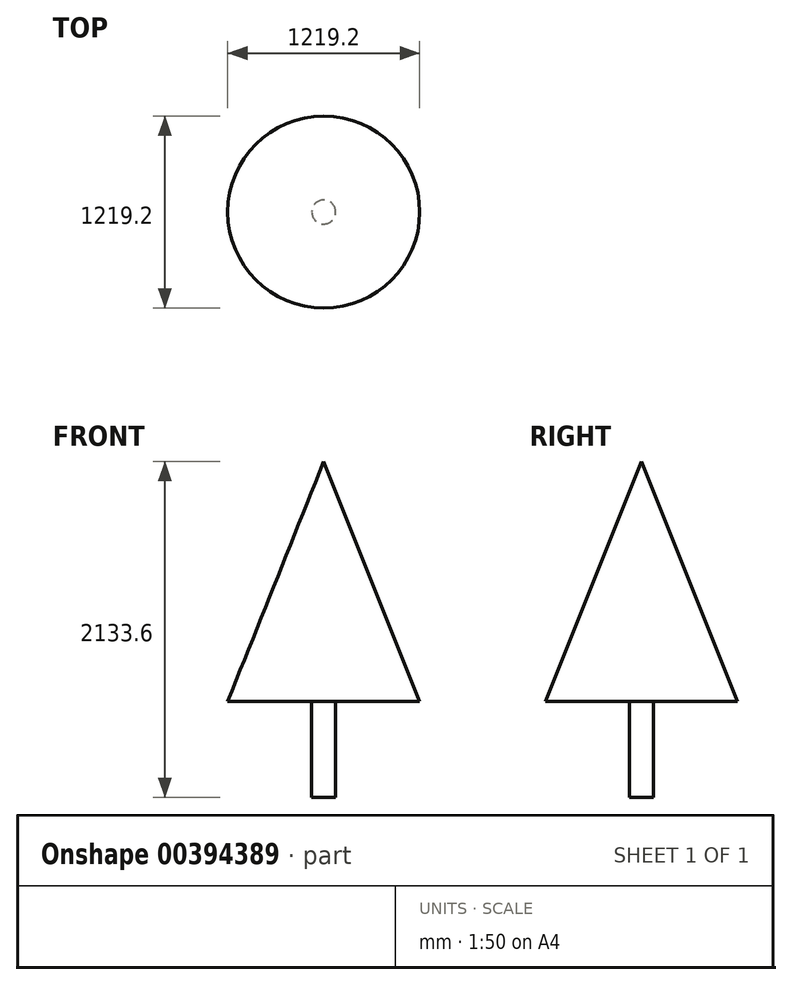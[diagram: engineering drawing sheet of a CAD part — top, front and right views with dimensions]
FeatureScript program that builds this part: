
annotation { "Feature Type Name" : "Feature", "Feature Type Description" : "" }
export const myFeature = defineFeature(function(context is Context, id is Id, definition is map)
    precondition{}
    {
        {
            var Q0;
            Q0=qCreatedBy(makeId("Front.planeOp"),FACE);
            var sketch = newSketch(context, id + "F0", { "sketchPlane" : qUnion([Q0])});
            skLineSegment(sketch, "E0.bottom", {"start": v(0, 0) * mm, "end": v(76.2, 0) * mm});
            skLineSegment(sketch, "E0.top", {"start": v(0, -609.6) * mm, "end": v(76.2, -609.6) * mm});
            skLineSegment(sketch, "E0.left", {"start": v(0, 0) * mm, "end": v(0, -609.6) * mm});
            skLineSegment(sketch, "E0.right", {"start": v(76.2, 0) * mm, "end": v(76.2, -609.6) * mm});
            skLineSegment(sketch, "E1", {"start": v(0, 0) * mm, "end": v(609.6, 0) * mm});
            skPoint(sketch, "E1.endSnap0", {"position": v(38.1, 0) * mm});
            skLineSegment(sketch, "E2", {"start": v(0, 0) * mm, "end": v(0, 1524) * mm});
            skLineSegment(sketch, "E3", {"start": v(0, 1524) * mm, "end": v(609.6, 0) * mm});
            skSolve(sketch);
        }
        {
            var Q0;
            {var subQ0=sQuery(id+"F0.wireOp",EDGE,"E2");Q0=makeQuery(id+"F0.imprint","IMPRINT",FACE,{"disambiguationData":[TD([[makeQuery(id+"F0.imprint","IMPRINT",EDGE,{"derivedFrom":subQ0}),-1.0]])]});}
            var Q1;
            Q1=makeQuery(id+"F0.imprint","IMPRINT",FACE,{"disambiguationData":[TD([[makeQuery(id+"F0.imprint","IMPRINT",EDGE,{"derivedFrom":sQuery(id+"F0.wireOp",EDGE,"E0.top")}),1.0]])]});
            var Q2;
            Q2=sQuery(id+"F0.wireOp",EDGE,"E0.left");
            revolve(context, id + "F1", {"entities" : qUnion([Q0, Q1]), "axis" : qUnion([Q2]), "revolveType" : RevolveType.FULL});
        }
    });
